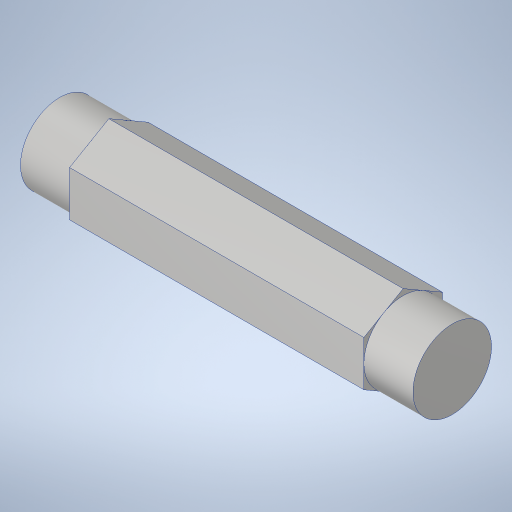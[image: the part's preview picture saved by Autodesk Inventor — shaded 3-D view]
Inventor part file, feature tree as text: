
AUTODESK INVENTOR PART (.ipt)
format: ipt  version: 2023.4 (Build 274418000, 418)  size: 261,632 bytes
history: native  units: in
note: dims shown in document units (in); Inventor stores cm internally (conversion verified against a paired STEP export)
features: extrude x3, sketch x3, projected_geometry x2
ambient origin geometry x8: Origin, YZ Plane, XZ Plane, XY Plane, X Axis, Y Axis, Z Axis, Center Point
bodies: Solid1 (feature_tree)
feature tree (8):
  extrude  "Extrusion1"  Depth=2.5in TaperAngle=0.0deg
  extrude  "Extrusion2"  Depth=0.3125in TaperAngle=0.0deg
  extrude  "Extrusion3"  Depth=0.3125in TaperAngle=0.0deg
  sketch  "Sketch1"  dims[d0=0.5in d1=2.5in d2=0.0in]
  sketch  "Sketch2"  dims[d3=0.5in d4=0.3125in d5=0.0in]
  projected_geometry  "Projected Loop1"
  sketch  "Sketch3"  dims[d6=0.5in d7=0.3125in d8=0.0in]
  projected_geometry  "Projected Loop2"
